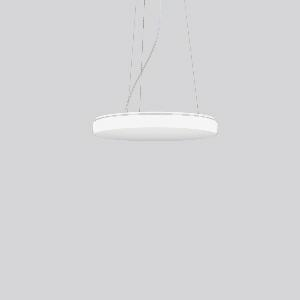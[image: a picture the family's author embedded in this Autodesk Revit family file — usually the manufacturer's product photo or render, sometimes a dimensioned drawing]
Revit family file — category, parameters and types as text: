
# Revit family: flat_polymero_kreis_slim_312091_002_3_ad95
name_source: partatom
category: Lighting Fixtures
units: mm (PartAtom-declared; Revit-internal decimal feet)

## family parameters
Cut with Voids When Loaded = No
Host = Face
Light Source = No
Part Type = Normal
Room Calculation Point = No
Round Connector Dimension = Use Diameter
Shared = No

## types (1)
- FLAT POLYMERO KREIS SLIM (1 x LED Modul 840, 3400 lm, 4000)
    Apparent Load = 28 VA
    CIE Flux Codes = 42 72 91 82 100
    Color Rendering = 80
    Color Temperature = 4000
    Default Elevation = 1800 mm
    Description = Series: FLAT POLYMERO KREIS SLIM
Decorative round LED pendant luminaire. Base and canopy: metal, powder-coated, white. Canopy Ø 205 mm, h 35 mm. Diffuser made of non-yellowing plastic (PMMA), opal. Diffuser fastening: patented push system. Homogeneous and smooth light distribution. Suitable for pendant. 3-point steel cable suspension, steplessly adjustable. Special lengths available on request. 
Colour: white
Diameter: 515 mm
Height: 69 mm
Suspension length: 350-1300 mm
Lamp: LED
Socket: without socket
Colour temperature: 4000K
Colour rendering index (CRI): 83
System power: 28 W
Rated luminous flux: 3400 lm
Luminous efficiency: 121 lm/W
Control gear: AC Strom, dim.Ph.an-/abschnitt
Protection class: I
Type of protection: IP 40
    Height = 69 mm
    Lamp = 1 x LED Modul 840
    Lamp Light Flux = 3400 lm
    Lamp count = 1
    Length = 515 mm
    Lifetime = 50000 h
    Luminous efficacy = 121 lm/W
    Manufacturer = RZB
    ModVariant = No
    Model = 312091.002.3
    Mounting Place = Ceiling
    Mounting Type = Pendant
    Number of Poles = 1
    OnlyDefault = Yes
    Power Factor = 1
    Product Name = FLAT POLYMERO KREIS SLIM
    Product group = Pendant luminaires
    ProductGroupID = 902
    Protection Class = Protection class I
    Protection Degree = IP 40
    RLX_Detail_Level = 1
    RLX_Emergency_Light_Flux = 0 lm
    RLX_Emergency_Type = 0
    RLX_Emergency_Type_DB = No
    RlxData = <blob elided: 42017 chars, md5=9d267343>
    Socket = socket
    Standby Power = 0 W
    System Light Flux = 3400 lm
    System Power = 28 W
    Type Comments = Product without accessories
    Type Image = 312091.002.jpg
    URL = http://relux.com
    VarID = ---
    Voltage = 230 V
    Voltage Range = 220-240 V
    Weight = 0.00 kg
    Width = 0 mm  [stored 0 ft]

note: [stored X ft] marks values corroborated as IEEE doubles in the binary element streams (Revit-internal decimal feet)

## geometry (parser evidence)
native form markers: Blend x4, Sweep x13
no freeform markers — native parametric forms only
